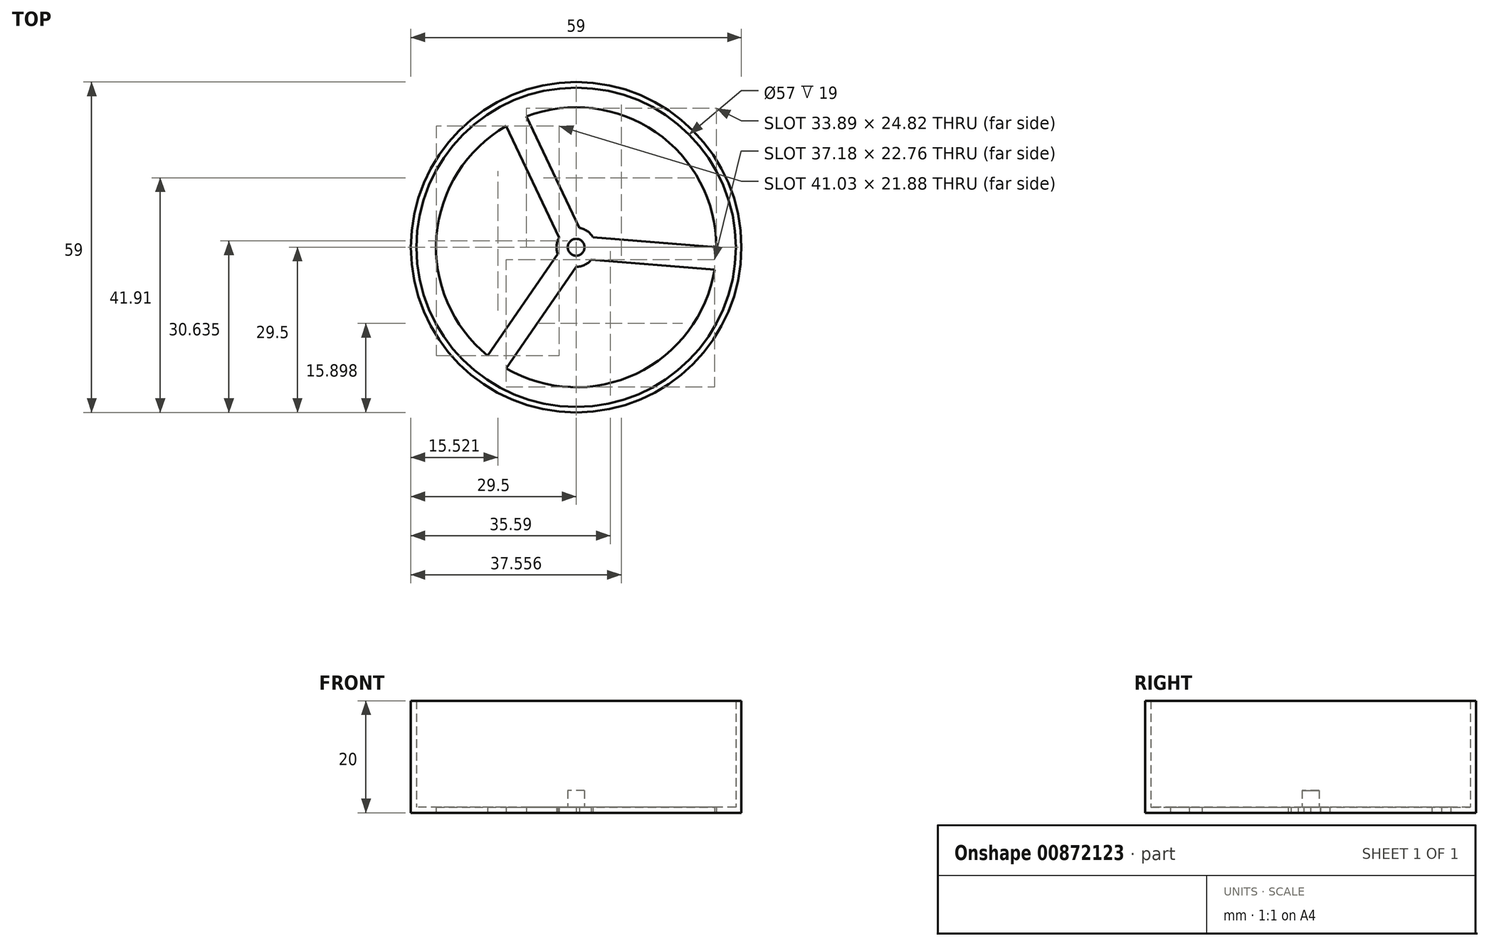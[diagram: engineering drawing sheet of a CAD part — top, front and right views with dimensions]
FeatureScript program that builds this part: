
annotation { "Feature Type Name" : "Feature", "Feature Type Description" : "" }
export const myFeature = defineFeature(function(context is Context, id is Id, definition is map)
    precondition{}
    {
        {
            var Q0;
            Q0=qCreatedBy(makeId("Top.planeOp"),FACE);
            var sketch = newSketch(context, id + "F0", { "sketchPlane" : qUnion([Q0])});
            skCircle(sketch, "E0", {"center": v(0, 0) * mm, "radius": 25 * mm});
            skCircle(sketch, "E1", {"center": v(0, 0) * mm, "radius": 29.5 * mm});
            skCircle(sketch, "E2", {"center": v(0, 0) * mm, "radius": 28.5 * mm});
            skCircle(sketch, "E3", {"center": v(0, 0) * mm, "radius": 3.5 * mm});
            skLineSegment(sketch, "E4", {"start": v(-12.5, -21.65) * mm, "end": v(0.01, -3.5) * mm});
            skLineSegment(sketch, "E5", {"start": v(-15.8, -19.38) * mm, "end": v(-3.28, -1.23) * mm});
            skLineSegment(sketch, "E6", {"start": v(-8.89, 23.37) * mm, "end": v(0.58, 3.45) * mm});
            skLineSegment(sketch, "E7", {"start": v(-12.5, 21.65) * mm, "end": v(-3.04, 1.74) * mm});
            skLineSegment(sketch, "E8", {"start": v(25, 0) * mm, "end": v(3.02, 1.76) * mm});
            skLineSegment(sketch, "E9", {"start": v(24.68, -3.99) * mm, "end": v(2.7, -2.22) * mm});
            skSolve(sketch);
        }
        {
            var Q0;
            Q0 = qSketchRegion(id + "F0", true);
            extrude(context, id + "F1", {"entities" : qUnion([Q0]), "depth" : 20 * mm, "offsetDistance" : 25 * mm});
        }
        {
            var Q0;
            Q0=makeQuery(id+"F0.imprint","IMPRINT",FACE,{"disambiguationData":[TD([[makeQuery(id+"F0.imprint","IMPRINT",EDGE,{"derivedFrom":sQuery(id+"F0.wireOp",EDGE,"E0")}),-1.0]])]});
            var Q1;
            {var subQ0=sQuery(id+"F0.wireOp",EDGE,"E6");Q1=makeQuery(id+"F0.imprint","IMPRINT",FACE,{"disambiguationData":[TD([[makeQuery(id+"F0.imprint","IMPRINT",EDGE,{"derivedFrom":subQ0}),-1.0]])]});}
            var Q2;
            {var subQ0=sQuery(id+"F0.wireOp",EDGE,"E4");Q2=makeQuery(id+"F0.imprint","IMPRINT",FACE,{"disambiguationData":[TD([[makeQuery(id+"F0.imprint","IMPRINT",EDGE,{"derivedFrom":subQ0}),1.0]])]});}
            var Q3;
            {var subQ0=sQuery(id+"F0.wireOp",EDGE,"E3");var subQ4=makeQuery(id+"F0.imprint","INTERSECT",VERTEX,{"derivedFrom":[subQ0,sQuery(id+"F0.wireOp",EDGE,"E6")]});Q3=makeQuery(id+"F0.imprint","IMPRINT",FACE,{"disambiguationData":[TD([[makeQuery(id+"F0.imprint","IMPRINT",EDGE,{"disambiguationData":[TD([[subQ4,1.0]])],"derivedFrom":subQ0}),1.0]])]});}
            var Q4;
            {var subQ0=sQuery(id+"F0.wireOp",EDGE,"E8");Q4=makeQuery(id+"F0.imprint","IMPRINT",FACE,{"disambiguationData":[TD([[makeQuery(id+"F0.imprint","IMPRINT",EDGE,{"derivedFrom":subQ0}),1.0]])]});}
            extrude(context, id + "F2", {"entities" : qUnion([Q0, Q1, Q2, Q3, Q4]), "operationType" : NewBodyOperationType.ADD, "depth" : 1 * mm, "offsetDistance" : 25 * mm});
        }
        {
            var Q0;
            Q0=makeQuery(id+"F2.opExtrude","CAP_FACE",FACE,{"disambiguationData":[OSD([sQuery(id+"F0.wireOp",EDGE,"E0"),sQuery(id+"F0.wireOp",EDGE,"E2"),sQuery(id+"F0.wireOp",EDGE,"E3"),sQuery(id+"F0.wireOp",EDGE,"E4"),sQuery(id+"F0.wireOp",EDGE,"E5"),sQuery(id+"F0.wireOp",EDGE,"E6"),sQuery(id+"F0.wireOp",EDGE,"E7"),sQuery(id+"F0.wireOp",EDGE,"E8"),sQuery(id+"F0.wireOp",EDGE,"E9")])],"isStart":false});
            var sketch = newSketch(context, id + "F3", { "sketchPlane" : qUnion([Q0])});
            skCircle(sketch, "E10", {"center": v(0, 0) * mm, "radius": 1.5 * mm});
            skSolve(sketch);
        }
        {
            var Q0;
            Q0=makeQuery(id+"F3.imprint","IMPRINT",FACE,{"disambiguationData":[TD([[makeQuery(id+"F3.imprint","IMPRINT",EDGE,{"derivedFrom":sQuery(id+"F3.wireOp",EDGE,"E10")}),1.0]])]});
            extrude(context, id + "F4", {"entities" : qUnion([Q0]), "operationType" : NewBodyOperationType.ADD, "depth" : 3 * mm, "offsetDistance" : 25 * mm});
        }
    });
